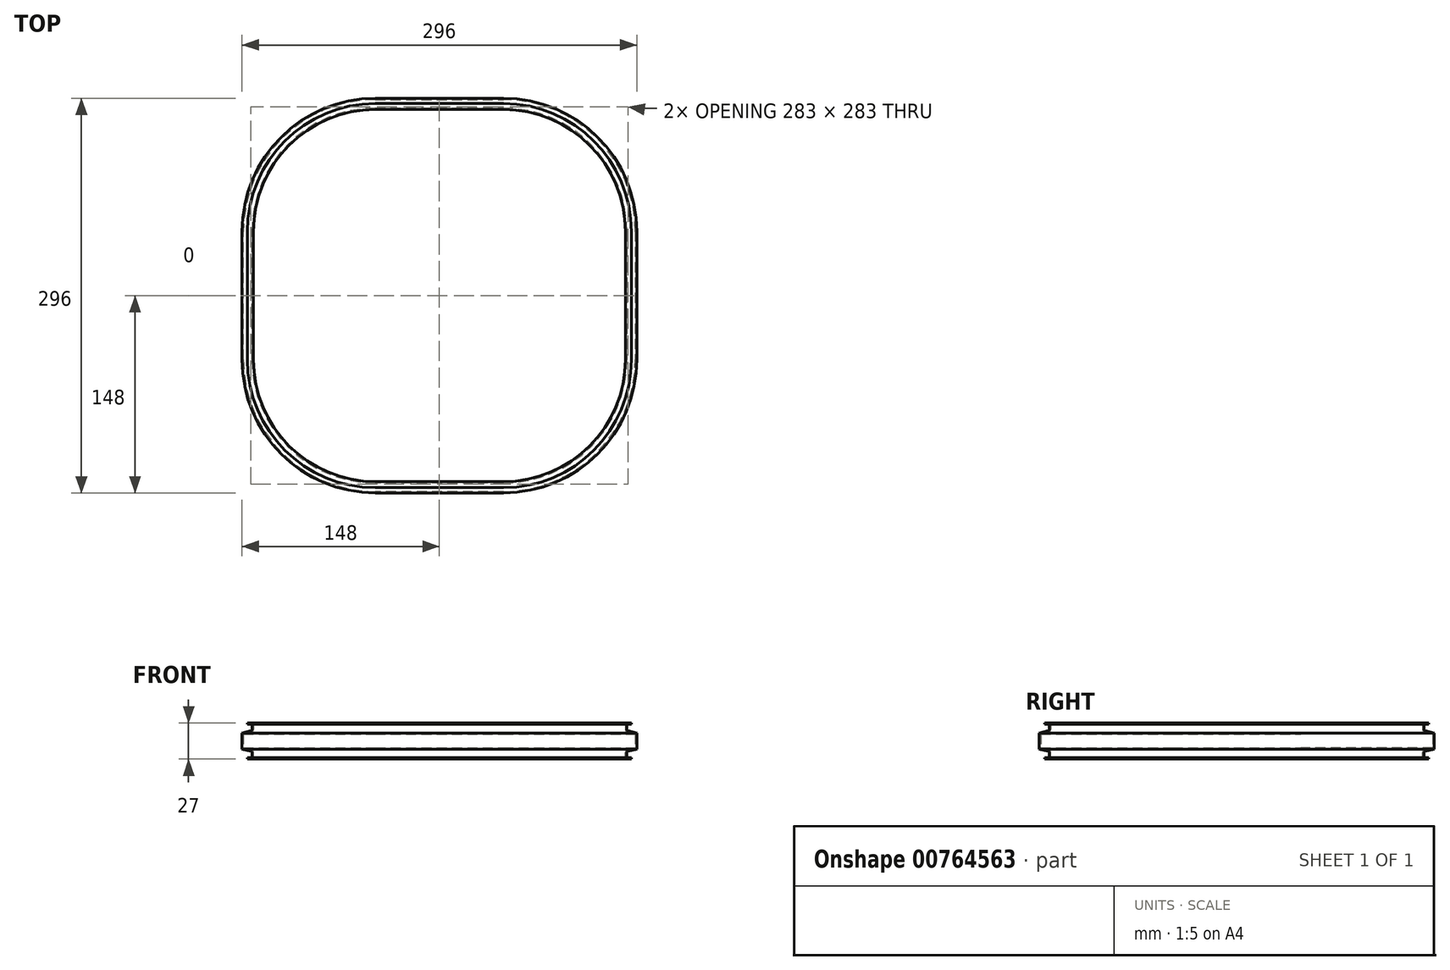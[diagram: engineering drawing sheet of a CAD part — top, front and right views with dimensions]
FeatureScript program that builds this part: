
annotation { "Feature Type Name" : "Feature", "Feature Type Description" : "" }
export const myFeature = defineFeature(function(context is Context, id is Id, definition is map)
    precondition{}
    {
        {
            var Q0;
            Q0=qCreatedBy(makeId("Top.planeOp"),FACE);
            var sketch = newSketch(context, id + "F0", { "sketchPlane" : qUnion([Q0])});
            skLineSegment(sketch, "E0.bottom", {"start": v(-48, 148) * mm, "end": v(48, 148) * mm});
            skLineSegment(sketch, "E0.top", {"start": v(-48, -148) * mm, "end": v(48, -148) * mm});
            skLineSegment(sketch, "E0.left", {"start": v(-148, 48) * mm, "end": v(-148, -48) * mm});
            skLineSegment(sketch, "E0.right", {"start": v(148, 48) * mm, "end": v(148, -48) * mm});
            skPoint(sketch, "E1.visualSharp", {"position": v(148, 148) * mm});
            skArc(sketch, "E1.filletArc", {"start": v(148, 48) * mm, "mid": v(118.71, 118.71) * mm, "end": v(48, 148) * mm});
            skPoint(sketch, "E2.visualSharp", {"position": v(-148, 148) * mm});
            skArc(sketch, "E2.filletArc", {"start": v(-48, 148) * mm, "mid": v(-118.71, 118.71) * mm, "end": v(-148, 48) * mm});
            skPoint(sketch, "E3.visualSharp", {"position": v(-148, -148) * mm});
            skArc(sketch, "E3.filletArc", {"start": v(-148, -48) * mm, "mid": v(-118.71, -118.71) * mm, "end": v(-48, -148) * mm});
            skPoint(sketch, "E4.visualSharp", {"position": v(148, -148) * mm});
            skArc(sketch, "E4.filletArc", {"start": v(48, -148) * mm, "mid": v(118.71, -118.71) * mm, "end": v(148, -48) * mm});
            skSolve(sketch);
        }
        {
            var Q0;
            Q0=qCreatedBy(makeId("Front.planeOp"),FACE);
            var sketch = newSketch(context, id + "F1", { "sketchPlane" : qUnion([Q0])});
            skLineSegment(sketch, "E5", {"start": v(148, 6) * mm, "end": v(148, -34.3) * mm, "construction": true});
            skLineSegment(sketch, "E6", {"start": v(148, 6) * mm, "end": v(141.24, 7.81) * mm});
            skLineSegment(sketch, "E7", {"start": v(140.5, 8.78) * mm, "end": v(140.5, 11.5) * mm});
            skLineSegment(sketch, "E8", {"start": v(141.5, 12.5) * mm, "end": v(144, 12.5) * mm});
            skLineSegment(sketch, "E9", {"start": v(144, 12.5) * mm, "end": v(144, 13.5) * mm});
            skLineSegment(sketch, "E10", {"start": v(144, 13.5) * mm, "end": v(141.5, 13.5) * mm});
            skLineSegment(sketch, "E11", {"start": v(139.5, 11.5) * mm, "end": v(139.5, 8.78) * mm});
            skLineSegment(sketch, "E12", {"start": v(140.98, 6.85) * mm, "end": v(147, 5.23) * mm});
            skLineSegment(sketch, "E13", {"start": v(147, 5.23) * mm, "end": v(147, 0) * mm});
            skLineSegment(sketch, "E14", {"start": v(148, 6) * mm, "end": v(154.26, 6) * mm, "construction": true});
            skPoint(sketch, "E15.visualSharp", {"position": v(140.5, 12.5) * mm});
            skArc(sketch, "E15.filletArc", {"start": v(141.5, 12.5) * mm, "mid": v(140.8, 12.2) * mm, "end": v(140.5, 11.5) * mm});
            skPoint(sketch, "E16.visualSharp", {"position": v(140.5, 8) * mm});
            skArc(sketch, "E16.filletArc", {"start": v(140.5, 8.78) * mm, "mid": v(140.7, 8.17) * mm, "end": v(141.24, 7.81) * mm});
            skPoint(sketch, "E17.visualSharp", {"position": v(139.5, 13.5) * mm});
            skArc(sketch, "E17.filletArc", {"start": v(141.5, 13.5) * mm, "mid": v(140.09, 12.91) * mm, "end": v(139.5, 11.5) * mm});
            skPoint(sketch, "E18.visualSharp", {"position": v(139.5, 7.24) * mm});
            skArc(sketch, "E18.filletArc", {"start": v(139.5, 8.78) * mm, "mid": v(139.91, 7.56) * mm, "end": v(140.98, 6.85) * mm});
            skArc(sketch, "E19.MirrorCS", {"start": v(139.5, -8.78) * mm, "mid": v(139.91, -7.56) * mm, "end": v(140.98, -6.85) * mm});
            skLineSegment(sketch, "E20.MirrorCS", {"start": v(140.5, -8.78) * mm, "end": v(140.5, -11.5) * mm});
            skArc(sketch, "E21.MirrorCS", {"start": v(140.5, -8.78) * mm, "mid": v(140.7, -8.17) * mm, "end": v(141.24, -7.81) * mm});
            skArc(sketch, "E22.MirrorCS", {"start": v(141.5, -12.5) * mm, "mid": v(140.8, -12.2) * mm, "end": v(140.5, -11.5) * mm});
            skLineSegment(sketch, "E23.MirrorCS", {"start": v(139.5, -11.5) * mm, "end": v(139.5, -8.78) * mm});
            skArc(sketch, "E24.MirrorCS", {"start": v(141.5, -13.5) * mm, "mid": v(140.09, -12.91) * mm, "end": v(139.5, -11.5) * mm});
            skLineSegment(sketch, "E25.MirrorCS", {"start": v(141.5, -12.5) * mm, "end": v(144, -12.5) * mm});
            skLineSegment(sketch, "E26.MirrorCS", {"start": v(144, -12.5) * mm, "end": v(144, -13.5) * mm});
            skLineSegment(sketch, "E27.MirrorCS", {"start": v(144, -13.5) * mm, "end": v(141.5, -13.5) * mm});
            skLineSegment(sketch, "E28.MirrorCS", {"start": v(148, -6) * mm, "end": v(141.24, -7.81) * mm});
            skPoint(sketch, "E29.MirrorP", {"position": v(140.5, -8) * mm});
            skLineSegment(sketch, "E30.MirrorCS", {"start": v(140.98, -6.85) * mm, "end": v(147, -5.23) * mm});
            skLineSegment(sketch, "E31.MirrorCS", {"start": v(148, -6) * mm, "end": v(154.26, -6) * mm, "construction": true});
            skPoint(sketch, "E32.MirrorP", {"position": v(139.5, -7.24) * mm});
            skPoint(sketch, "E33.MirrorP", {"position": v(139.5, -13.5) * mm});
            skPoint(sketch, "E34.MirrorP", {"position": v(140.5, -12.5) * mm});
            skLineSegment(sketch, "E35.MirrorCS", {"start": v(148, -6) * mm, "end": v(148, 34.3) * mm, "construction": true});
            skLineSegment(sketch, "E36.MirrorCS", {"start": v(147, -5.23) * mm, "end": v(147, 0) * mm});
            skLineSegment(sketch, "E37", {"start": v(148, 6) * mm, "end": v(148, -6) * mm});
            skSolve(sketch);
        }
        {
            var Q0;
            Q0 = qSketchRegion(id + "F1", true);
            var Q1;
            Q1=sQuery(id+"F0.wireOp",EDGE,"E0.right");
            var Q2;
            Q2=sQuery(id+"F0.wireOp",EDGE,"E1.filletArc");
            var Q3;
            Q3=sQuery(id+"F0.wireOp",EDGE,"E0.bottom");
            var Q4;
            Q4=sQuery(id+"F0.wireOp",EDGE,"E2.filletArc");
            var Q5;
            Q5=sQuery(id+"F0.wireOp",EDGE,"E0.left");
            var Q6;
            Q6=sQuery(id+"F0.wireOp",EDGE,"E3.filletArc");
            var Q7;
            Q7=sQuery(id+"F0.wireOp",EDGE,"E0.top");
            var Q8;
            Q8=sQuery(id+"F0.wireOp",EDGE,"E4.filletArc");
            sweep(context, id + "F2", {"profiles" : qUnion([Q0]), "path" : qUnion([Q1, Q2, Q3, Q4, Q5, Q6, Q7, Q8])});
        }
    });
